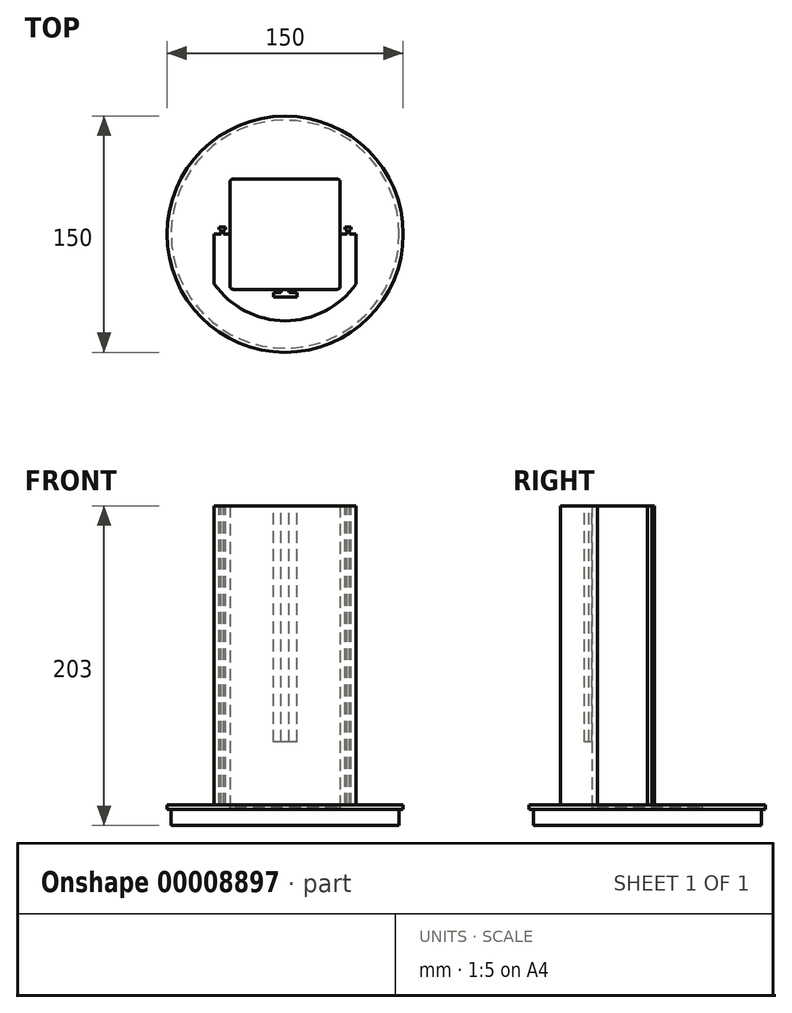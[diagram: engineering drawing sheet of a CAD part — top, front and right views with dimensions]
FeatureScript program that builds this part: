
annotation { "Feature Type Name" : "Feature", "Feature Type Description" : "" }
export const myFeature = defineFeature(function(context is Context, id is Id, definition is map)
    precondition{}
    {
        {
            var Q0;
            Q0=qCreatedBy(makeId("Top.planeOp"),FACE);
            var sketch = newSketch(context, id + "F0", { "sketchPlane" : qUnion([Q0])});
            skCircle(sketch, "E0", {"center": v(0, 0) * mm, "radius": 75 * mm});
            skSolve(sketch);
        }
        {
            var Q0;
            Q0=makeQuery(id+"F0.imprint","IMPRINT",FACE,{"disambiguationData":[TD([[makeQuery(id+"F0.imprint","IMPRINT",EDGE,{"derivedFrom":sQuery(id+"F0.wireOp",EDGE,"E0")}),1.0]])]});
            extrude(context, id + "F1", {"entities" : qUnion([Q0]), "oppositeDirection" : true, "depth" : 13 * mm});
        }
        {
            var Q0;
            Q0=makeQuery(id+"F1.opExtrude","CAP_FACE",FACE,{"disambiguationData":[OSD([sQuery(id+"F0.wireOp",EDGE,"E0")])],"isStart":true});
            var sketch = newSketch(context, id + "F2", { "sketchPlane" : qUnion([Q0])});
            skSolve(sketch);
        }
        {
            var Q0;
            Q0=makeQuery(id+"F2.imprint","IMPRINT",FACE,{"disambiguationData":[TD([[makeQuery(id+"F2.imprint","IMPRINT",EDGE,{"derivedFrom":makeQuery(id+"F1.opExtrude","CAP_EDGE",EDGE,{"disambiguationData":[OSD([sQuery(id+"F0.wireOp",EDGE,"E0")])],"isStart":true})}),1.0]])]});
            var sketch = newSketch(context, id + "F3", { "sketchPlane" : qUnion([Q0])});
            skLineSegment(sketch, "E1", {"start": v(55, 0) * mm, "end": v(-55, 0) * mm});
            skLineSegment(sketch, "E2", {"start": v(0, 0) * mm, "end": v(0, -35) * mm});
            skLineSegment(sketch, "E3", {"start": v(33, -35) * mm, "end": v(-33, -35) * mm});
            skLineSegment(sketch, "E4.0", {"start": v(-35, 0) * mm, "end": v(-35, -33) * mm});
            skLineSegment(sketch, "E5.0", {"start": v(35, 0) * mm, "end": v(35, -33) * mm});
            skArc(sketch, "E6.filletArc", {"start": v(-35, -33) * mm, "mid": v(-34.41, -34.41) * mm, "end": v(-33, -35) * mm});
            skArc(sketch, "E7.filletArc", {"start": v(33, -35) * mm, "mid": v(34.41, -34.41) * mm, "end": v(35, -33) * mm});
            skLineSegment(sketch, "E8.0", {"start": v(-45, 0) * mm, "end": v(-45, -31.62) * mm});
            skLineSegment(sketch, "E9.0", {"start": v(45, 0) * mm, "end": v(45, -31.62) * mm});
            skLineSegment(sketch, "E10.0.MirrorCS", {"start": v(35, 0) * mm, "end": v(35, 33) * mm});
            skLineSegment(sketch, "E11.0.MirrorCS", {"start": v(0, 0) * mm, "end": v(0, 35) * mm});
            skLineSegment(sketch, "E12.0.MirrorCS", {"start": v(-35, 0) * mm, "end": v(-35, 33) * mm});
            skArc(sketch, "E13.0.MirrorCS", {"start": v(-35, 33) * mm, "mid": v(-34.41, 34.41) * mm, "end": v(-33, 35) * mm});
            skArc(sketch, "E14.0.MirrorCS", {"start": v(33, 35) * mm, "mid": v(34.41, 34.41) * mm, "end": v(35, 33) * mm});
            skLineSegment(sketch, "E15.0.MirrorCS", {"start": v(33, 35) * mm, "end": v(-33, 35) * mm});
            skCircle(sketch, "E16.0", {"center": v(0, 0) * mm, "radius": 55 * mm});
            skSolve(sketch);
        }
        {
            var Q0;
            {var subQ5=sQuery(id+"F3.wireOp",EDGE,"E4.0");Q0=makeQuery(id+"F3.imprint","IMPRINT",FACE,{"disambiguationData":[TD([[makeQuery(id+"F3.imprint","IMPRINT",EDGE,{"derivedFrom":subQ5}),-1.0]])]});}
            extrude(context, id + "F4", {"entities" : qUnion([Q0]), "operationType" : NewBodyOperationType.ADD, "depth" : 190 * mm});
        }
        {
            var Q0;
            Q0=makeQuery(id+"F4.opExtrude","CAP_FACE",FACE,{"disambiguationData":[OSD([sQuery(id+"F3.wireOp",EDGE,"E1"),sQuery(id+"F3.wireOp",EDGE,"E3"),sQuery(id+"F3.wireOp",EDGE,"E4.0"),sQuery(id+"F3.wireOp",EDGE,"E5.0"),sQuery(id+"F3.wireOp",EDGE,"E6.filletArc"),sQuery(id+"F3.wireOp",EDGE,"E7.filletArc"),sQuery(id+"F3.wireOp",EDGE,"E8.0"),sQuery(id+"F3.wireOp",EDGE,"E9.0"),sQuery(id+"F3.wireOp",EDGE,"30718d8a-f85b-44eb-b5a2-9b228f8a43ee.trimOffspring")])],"isStart":false});
            var sketch = newSketch(context, id + "F5", { "sketchPlane" : qUnion([Q0])});
            skLineSegment(sketch, "E17", {"start": v(-45, 0) * mm, "end": v(-45, 5) * mm});
            skLineSegment(sketch, "E18", {"start": v(45, 0) * mm, "end": v(45, 5) * mm});
            skLineSegment(sketch, "E19.0", {"start": v(-37.5, 2.5) * mm, "end": v(-37.5, 5) * mm});
            skLineSegment(sketch, "E20.0", {"start": v(-38.75, 0) * mm, "end": v(-38.75, 2.5) * mm});
            skLineSegment(sketch, "E21.0", {"start": v(-42.5, 2.5) * mm, "end": v(-42.5, 5) * mm});
            skLineSegment(sketch, "E22.0", {"start": v(-41.25, 0) * mm, "end": v(-41.25, 2.5) * mm});
            skLineSegment(sketch, "E23.0", {"start": v(42.5, 2.5) * mm, "end": v(42.5, 5) * mm});
            skLineSegment(sketch, "E24.0", {"start": v(37.5, 2.5) * mm, "end": v(37.5, 5) * mm});
            skLineSegment(sketch, "E25.0", {"start": v(41.25, 0) * mm, "end": v(41.25, 2.5) * mm});
            skLineSegment(sketch, "E26.0", {"start": v(38.75, 0) * mm, "end": v(38.75, 2.5) * mm});
            skLineSegment(sketch, "E27", {"start": v(42.5, 5) * mm, "end": v(37.5, 5) * mm});
            skLineSegment(sketch, "E28", {"start": v(-42.5, 5) * mm, "end": v(-37.5, 5) * mm});
            skLineSegment(sketch, "E29.0", {"start": v(-42.5, 2.5) * mm, "end": v(-41.25, 2.5) * mm});
            skLineSegment(sketch, "E30.trimOffspring", {"start": v(-38.75, 2.5) * mm, "end": v(-37.5, 2.5) * mm});
            skLineSegment(sketch, "E31.0", {"start": v(42.5, 2.5) * mm, "end": v(41.25, 2.5) * mm});
            skLineSegment(sketch, "E32.trimOffspring", {"start": v(38.75, 2.5) * mm, "end": v(37.5, 2.5) * mm});
            skLineSegment(sketch, "E33.0", {"start": v(-42.5, 4.5) * mm, "end": v(-37.5, 4.5) * mm});
            skLineSegment(sketch, "E34.0", {"start": v(-42, 2.5) * mm, "end": v(-42, 5) * mm});
            skLineSegment(sketch, "E35.0", {"start": v(-38, 2.5) * mm, "end": v(-38, 5) * mm});
            skLineSegment(sketch, "E36.0", {"start": v(-42.5, 3) * mm, "end": v(-40.75, 3) * mm});
            skLineSegment(sketch, "E37.0", {"start": v(-39.25, 3) * mm, "end": v(-37.5, 3) * mm});
            skLineSegment(sketch, "E38.0", {"start": v(-40.75, 0) * mm, "end": v(-40.75, 3) * mm});
            skLineSegment(sketch, "E39.0", {"start": v(-39.25, 0) * mm, "end": v(-39.25, 3) * mm});
            skLineSegment(sketch, "E40.0", {"start": v(42.5, 4.5) * mm, "end": v(37.5, 4.5) * mm});
            skLineSegment(sketch, "E41.0", {"start": v(38, 2.5) * mm, "end": v(38, 5) * mm});
            skLineSegment(sketch, "E42.0", {"start": v(42, 2.5) * mm, "end": v(42, 5) * mm});
            skLineSegment(sketch, "E43.0", {"start": v(42.5, 3) * mm, "end": v(40.75, 3) * mm});
            skLineSegment(sketch, "E44.0", {"start": v(39.25, 3) * mm, "end": v(37.5, 3) * mm});
            skLineSegment(sketch, "E45.0", {"start": v(39.25, 0) * mm, "end": v(39.25, 3) * mm});
            skLineSegment(sketch, "E46.0", {"start": v(40.75, 0) * mm, "end": v(40.75, 3) * mm});
            skSolve(sketch);
        }
        {
            var Q0;
            {var subQ1=sQuery(id+"F5.wireOp",EDGE,"E45.0");Q0=makeQuery(id+"F5.imprint","IMPRINT",FACE,{"disambiguationData":[TD([[makeQuery(id+"F5.imprint","IMPRINT",EDGE,{"derivedFrom":subQ1}),-1.0]])]});}
            var Q1;
            {var subQ3=sQuery(id+"F5.wireOp",EDGE,"E38.0");Q1=makeQuery(id+"F5.imprint","IMPRINT",FACE,{"disambiguationData":[TD([[makeQuery(id+"F5.imprint","IMPRINT",EDGE,{"derivedFrom":subQ3}),-1.0]])]});}
            extrude(context, id + "F6", {"entities" : qUnion([Q0, Q1]), "operationType" : NewBodyOperationType.ADD, "oppositeDirection" : true, "depth" : 200 * mm});
        }
        {
            var Q0;
            {var subQ0=sQuery(id+"F3.wireOp",EDGE,"E1");Q0=makeQuery(id+"F6.boolean.opBoolean","MERGE",FACE,{"derivedFrom":[makeQuery(id+"F4.opExtrude","CAP_FACE",FACE,{"disambiguationData":[OSD([subQ0,sQuery(id+"F3.wireOp",EDGE,"E3"),sQuery(id+"F3.wireOp",EDGE,"E4.0"),sQuery(id+"F3.wireOp",EDGE,"E5.0"),sQuery(id+"F3.wireOp",EDGE,"E6.filletArc"),sQuery(id+"F3.wireOp",EDGE,"E7.filletArc"),sQuery(id+"F3.wireOp",EDGE,"E8.0"),sQuery(id+"F3.wireOp",EDGE,"E9.0"),sQuery(id+"F3.wireOp",EDGE,"30718d8a-f85b-44eb-b5a2-9b228f8a43ee.trimOffspring")])],"isStart":false}),makeQuery(id+"F6.opExtrude","CAP_FACE",FACE,{"disambiguationData":[OSD([subQ0,sQuery(id+"F5.wireOp",EDGE,"E33.0"),sQuery(id+"F5.wireOp",EDGE,"E34.0"),sQuery(id+"F5.wireOp",EDGE,"E35.0"),sQuery(id+"F5.wireOp",EDGE,"E36.0"),sQuery(id+"F5.wireOp",EDGE,"E37.0"),sQuery(id+"F5.wireOp",EDGE,"E38.0"),sQuery(id+"F5.wireOp",EDGE,"E39.0")])],"isStart":true}),makeQuery(id+"F6.opExtrude","CAP_FACE",FACE,{"disambiguationData":[OSD([subQ0,sQuery(id+"F5.wireOp",EDGE,"E40.0"),sQuery(id+"F5.wireOp",EDGE,"E41.0"),sQuery(id+"F5.wireOp",EDGE,"E42.0"),sQuery(id+"F5.wireOp",EDGE,"E43.0"),sQuery(id+"F5.wireOp",EDGE,"E44.0"),sQuery(id+"F5.wireOp",EDGE,"E45.0"),sQuery(id+"F5.wireOp",EDGE,"E46.0")])],"isStart":true})]});}
            var sketch = newSketch(context, id + "F7", { "sketchPlane" : qUnion([Q0])});
            skLineSegment(sketch, "E47", {"start": v(-35, -33) * mm, "end": v(-35, -42.04) * mm});
            skLineSegment(sketch, "E48", {"start": v(35, -33) * mm, "end": v(35, -41.78) * mm});
            skLineSegment(sketch, "E49", {"start": v(-33, -35) * mm, "end": v(33, -35) * mm});
            skLineSegment(sketch, "E50.0", {"start": v(-2.5, -35) * mm, "end": v(-2.5, -37) * mm});
            skLineSegment(sketch, "E51.0", {"start": v(2.5, -35) * mm, "end": v(2.5, -37) * mm});
            skPoint(sketch, "E52.0.end.orphan", {"position": v(0, -40) * mm});
            skLineSegment(sketch, "E53.0", {"start": v(-7.5, -37) * mm, "end": v(-7.5, -40) * mm});
            skLineSegment(sketch, "E54.0", {"start": v(7.5, -37) * mm, "end": v(7.5, -40) * mm});
            skPoint(sketch, "E55.start.orphan", {"position": v(0, -35) * mm});
            skLineSegment(sketch, "E56", {"start": v(-2.5, -35) * mm, "end": v(-7.5, -35) * mm});
            skLineSegment(sketch, "E57", {"start": v(7.5, -35) * mm, "end": v(2.5, -35) * mm});
            skLineSegment(sketch, "E58.0", {"start": v(7.5, -37) * mm, "end": v(2.5, -37) * mm});
            skLineSegment(sketch, "E59.trimOffspring", {"start": v(-2.5, -37) * mm, "end": v(-7.5, -37) * mm});
            skLineSegment(sketch, "E60.0", {"start": v(-2.5, -40) * mm, "end": v(-7.5, -40) * mm});
            skLineSegment(sketch, "E61.0", {"start": v(7.5, -40) * mm, "end": v(2.5, -40) * mm});
            skLineSegment(sketch, "E62", {"start": v(-2.5, -40) * mm, "end": v(2.5, -40) * mm});
            skSolve(sketch);
        }
        {
            var Q0;
            {var subQ1=sQuery(id+"F7.wireOp",EDGE,"E50.0");Q0=makeQuery(id+"F7.imprint","IMPRINT",FACE,{"disambiguationData":[TD([[makeQuery(id+"F7.imprint","IMPRINT",EDGE,{"derivedFrom":subQ1}),1.0]])]});}
            extrude(context, id + "F8", {"entities" : qUnion([Q0]), "operationType" : NewBodyOperationType.REMOVE, "oppositeDirection" : true, "depth" : 150 * mm});
        }
        {
            var Q0;
            {var subQ3=sQuery(id+"F3.wireOp",EDGE,"E2");Q0=makeQuery(id+"F3.imprint","IMPRINT",FACE,{"disambiguationData":[TD([[makeQuery(id+"F3.imprint","IMPRINT",EDGE,{"derivedFrom":subQ3}),1.0]])]});}
            var Q1;
            {var subQ3=sQuery(id+"F3.wireOp",EDGE,"E2");Q1=makeQuery(id+"F3.imprint","IMPRINT",FACE,{"disambiguationData":[TD([[makeQuery(id+"F3.imprint","IMPRINT",EDGE,{"derivedFrom":subQ3}),-1.0]])]});}
            var Q2;
            {var subQ2=sQuery(id+"F3.wireOp",EDGE,"E11.0.MirrorCS");Q2=makeQuery(id+"F3.imprint","IMPRINT",FACE,{"disambiguationData":[TD([[makeQuery(id+"F3.imprint","IMPRINT",EDGE,{"derivedFrom":subQ2}),1.0]])]});}
            var Q3;
            {var subQ3=sQuery(id+"F3.wireOp",EDGE,"E10.0.MirrorCS");Q3=makeQuery(id+"F3.imprint","IMPRINT",FACE,{"disambiguationData":[TD([[makeQuery(id+"F3.imprint","IMPRINT",EDGE,{"derivedFrom":subQ3}),1.0]])]});}
            extrude(context, id + "F9", {"entities" : qUnion([Q0, Q1, Q2, Q3]), "operationType" : NewBodyOperationType.REMOVE, "oppositeDirection" : true, "depth" : 2 * mm});
        }
        {
            var Q0;
            Q0=makeQuery(id+"F1.opExtrude","CAP_FACE",FACE,{"disambiguationData":[OSD([sQuery(id+"F0.wireOp",EDGE,"E0")])],"isStart":false});
            var sketch = newSketch(context, id + "F10", { "sketchPlane" : qUnion([Q0])});
            skCircle(sketch, "E63.0", {"center": v(0, 0) * mm, "radius": 72.4 * mm});
            skSolve(sketch);
        }
        {
            var Q0;
            Q0=makeQuery(id+"F10.imprint","IMPRINT",FACE,{"disambiguationData":[TD([[makeQuery(id+"F10.imprint","IMPRINT",EDGE,{"derivedFrom":sQuery(id+"F10.wireOp",EDGE,"E63.0")}),-1.0]])]});
            extrude(context, id + "F11", {"entities" : qUnion([Q0]), "operationType" : NewBodyOperationType.REMOVE, "oppositeDirection" : true, "depth" : 10 * mm});
        }
    });
